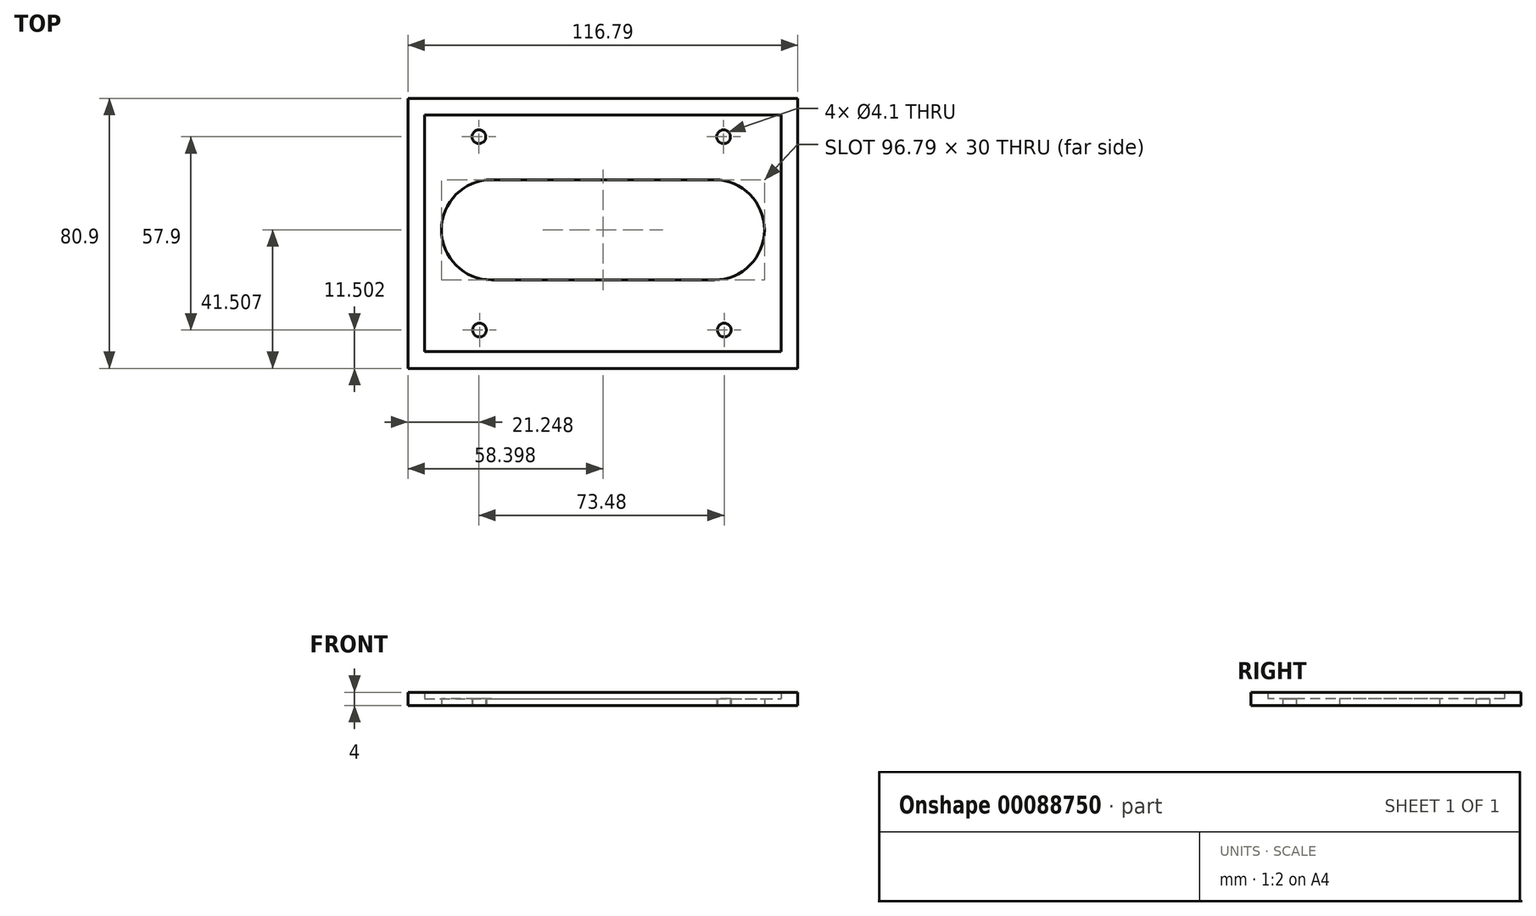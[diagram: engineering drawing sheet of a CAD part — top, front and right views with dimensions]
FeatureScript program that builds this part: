
annotation { "Feature Type Name" : "Feature", "Feature Type Description" : "" }
export const myFeature = defineFeature(function(context is Context, id is Id, definition is map)
    precondition{}
    {
        {
            var Q0;
            Q0=qCreatedBy(makeId("Top.planeOp"),FACE);
            var sketch = newSketch(context, id + "F0", { "sketchPlane" : qUnion([Q0])});
            skLineSegment(sketch, "E0.bottom", {"start": v(-63.49, 26.88) * mm, "end": v(43.3, 26.88) * mm});
            skLineSegment(sketch, "E0.top", {"start": v(-63.49, -44.02) * mm, "end": v(43.3, -44.02) * mm});
            skLineSegment(sketch, "E0.left", {"start": v(-63.49, 26.88) * mm, "end": v(-63.49, -44.02) * mm});
            skLineSegment(sketch, "E0.right", {"start": v(43.3, 26.88) * mm, "end": v(43.3, -44.02) * mm});
            skCircle(sketch, "E1", {"center": v(-47.24, 20.38) * mm, "radius": 2.05 * mm});
            skCircle(sketch, "E2", {"center": v(-47.06, -37.52) * mm, "radius": 2.05 * mm});
            skCircle(sketch, "E3", {"center": v(26.24, -37.52) * mm, "radius": 2.05 * mm});
            skCircle(sketch, "E4", {"center": v(26.06, 20.38) * mm, "radius": 2.05 * mm});
            skLineSegment(sketch, "E5.bottom", {"start": v(-68.49, 31.88) * mm, "end": v(48.3, 31.88) * mm});
            skLineSegment(sketch, "E5.top", {"start": v(-68.49, -49.02) * mm, "end": v(48.3, -49.02) * mm});
            skLineSegment(sketch, "E5.left", {"start": v(-68.49, 31.88) * mm, "end": v(-68.49, -49.02) * mm});
            skLineSegment(sketch, "E5.right", {"start": v(48.3, 31.88) * mm, "end": v(48.3, -49.02) * mm});
            skLineSegment(sketch, "E6", {"start": v(-43.49, -7.51) * mm, "end": v(23.3, -7.51) * mm});
            skArc(sketch, "E7.0.startCap", {"start": v(-43.49, -22.51) * mm, "mid": v(-58.49, -7.51) * mm, "end": v(-43.49, 7.49) * mm});
            skArc(sketch, "E7.0.endCap", {"start": v(23.3, 7.49) * mm, "mid": v(38.3, -7.51) * mm, "end": v(23.3, -22.51) * mm});
            skLineSegment(sketch, "E7.0.left", {"start": v(-43.49, 7.49) * mm, "end": v(23.3, 7.49) * mm});
            skLineSegment(sketch, "E7.0.right", {"start": v(-43.49, -22.51) * mm, "end": v(23.3, -22.51) * mm});
            skSolve(sketch);
        }
        {
            var Q0;
            Q0=makeQuery(id+"F0.imprint","IMPRINT",FACE,{"disambiguationData":[TD([[makeQuery(id+"F0.imprint","IMPRINT",EDGE,{"derivedFrom":sQuery(id+"F0.wireOp",EDGE,"E0.bottom")}),-1.0]])]});
            extrude(context, id + "F1", {"entities" : qUnion([Q0]), "depth" : 2 * mm});
        }
        {
            var Q0;
            Q0 = qSketchRegion(id + "F0", true);
            extrude(context, id + "F2", {"entities" : qUnion([Q0]), "operationType" : NewBodyOperationType.ADD, "depth" : 4 * mm});
        }
    });
